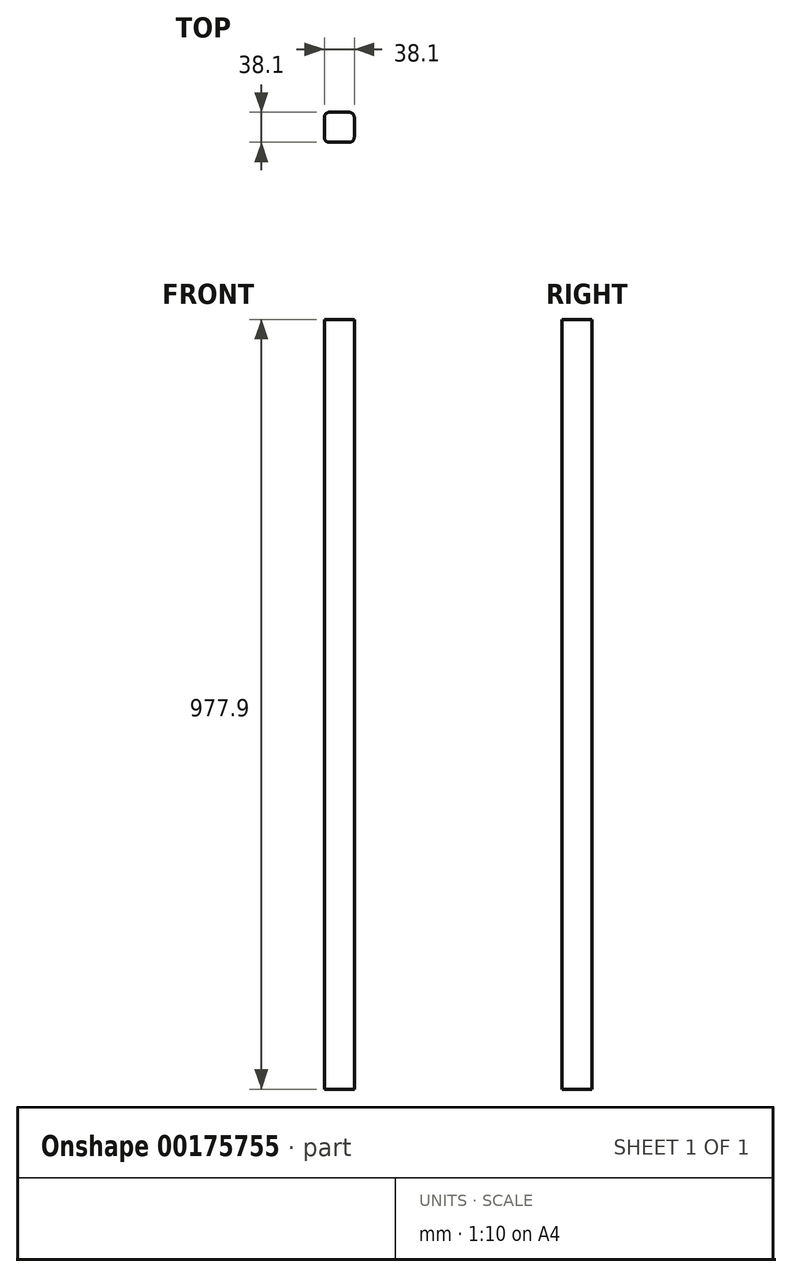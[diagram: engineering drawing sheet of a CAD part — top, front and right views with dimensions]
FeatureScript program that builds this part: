
annotation { "Feature Type Name" : "Feature", "Feature Type Description" : "" }
export const myFeature = defineFeature(function(context is Context, id is Id, definition is map)
    precondition{}
    {
        {
            var Q0;
            Q0=qCreatedBy(makeId("Top.planeOp"),FACE);
            var sketch = newSketch(context, id + "F0", { "sketchPlane" : qUnion([Q0])});
            skLineSegment(sketch, "E0.bottom", {"start": v(12.7, 19.05) * mm, "end": v(-12.7, 19.05) * mm});
            skLineSegment(sketch, "E0.top", {"start": v(12.7, -19.05) * mm, "end": v(-12.7, -19.05) * mm});
            skLineSegment(sketch, "E0.left", {"start": v(19.05, 12.7) * mm, "end": v(19.05, -12.7) * mm});
            skLineSegment(sketch, "E0.right", {"start": v(-19.05, 12.7) * mm, "end": v(-19.05, -12.7) * mm});
            skPoint(sketch, "E0.middle", {"position": v(0, 0) * mm});
            skPoint(sketch, "E1.visualSharp", {"position": v(-19.05, 19.05) * mm});
            skArc(sketch, "E1.filletArc", {"start": v(-12.7, 19.05) * mm, "mid": v(-17.2, 17.2) * mm, "end": v(-19.05, 12.7) * mm});
            skPoint(sketch, "E2.visualSharp", {"position": v(19.05, 19.05) * mm});
            skArc(sketch, "E2.filletArc", {"start": v(19.05, 12.7) * mm, "mid": v(17.2, 17.2) * mm, "end": v(12.7, 19.05) * mm});
            skPoint(sketch, "E3.visualSharp", {"position": v(19.05, -19.05) * mm});
            skArc(sketch, "E3.filletArc", {"start": v(12.7, -19.05) * mm, "mid": v(17.2, -17.2) * mm, "end": v(19.05, -12.7) * mm});
            skPoint(sketch, "E4.visualSharp", {"position": v(-19.05, -19.05) * mm});
            skArc(sketch, "E4.filletArc", {"start": v(-19.05, -12.7) * mm, "mid": v(-17.2, -17.2) * mm, "end": v(-12.7, -19.05) * mm});
            skSolve(sketch);
        }
        {
            var Q0;
            Q0=qSketchRegion(id+"F0",true);
            extrude(context, id + "F1", {"entities" : qUnion([Q0]), "depth" : 977.9 * mm, "offsetDistance" : 25.4 * mm});
        }
    });
